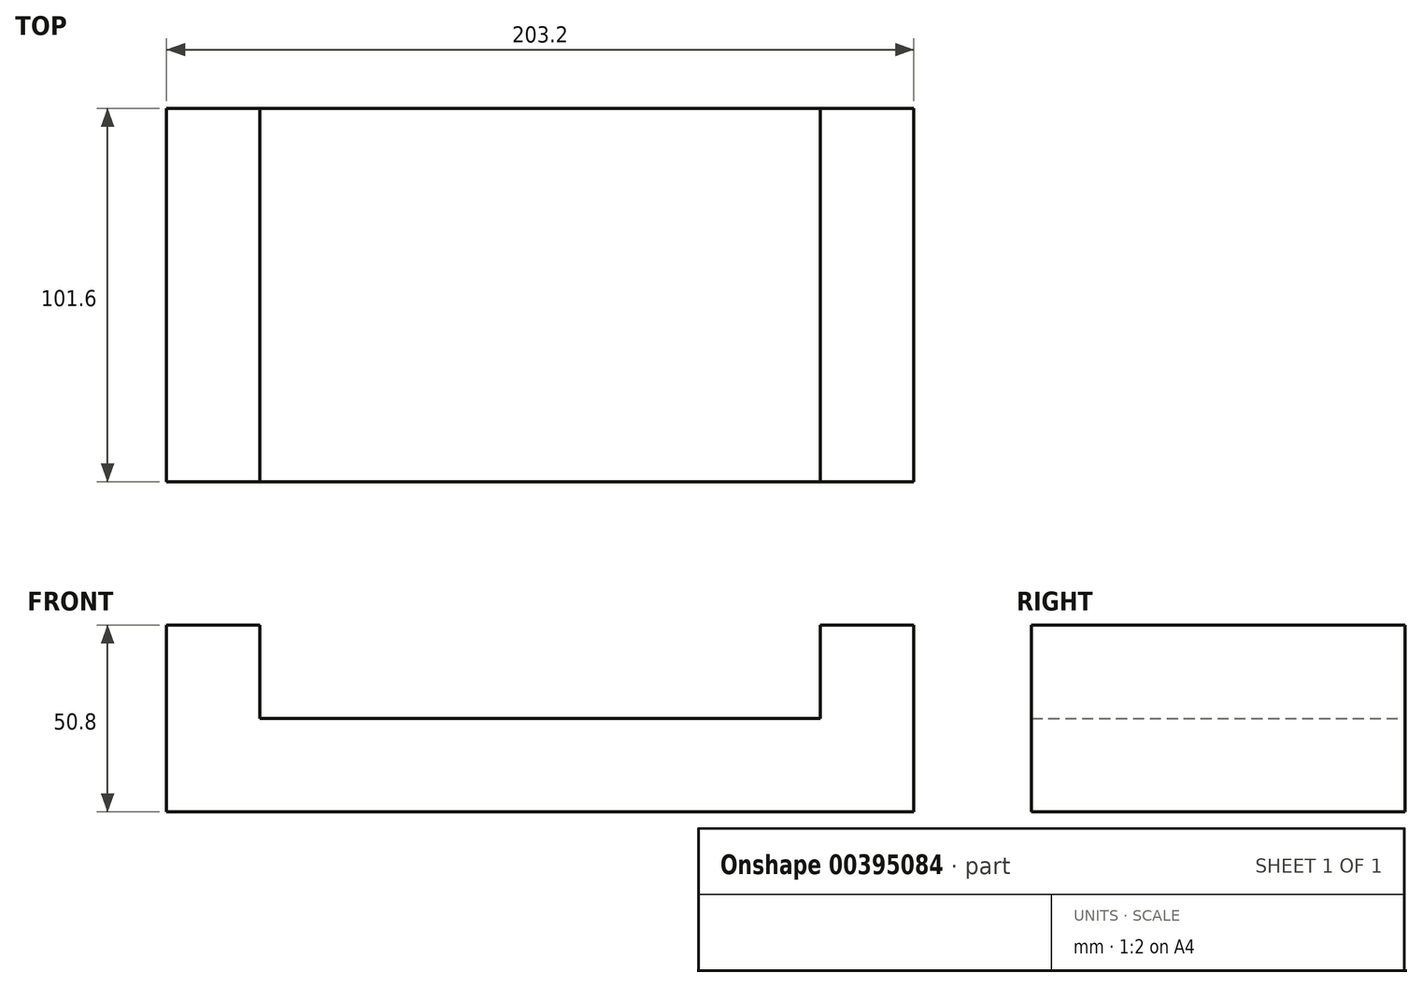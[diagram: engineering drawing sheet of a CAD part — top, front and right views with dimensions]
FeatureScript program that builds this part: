
annotation { "Feature Type Name" : "Feature", "Feature Type Description" : "" }
export const myFeature = defineFeature(function(context is Context, id is Id, definition is map)
    precondition{}
    {
        {
            var Q0;
            Q0=qCreatedBy(makeId("Front.planeOp"),FACE);
            var sketch = newSketch(context, id + "F0", { "sketchPlane" : qUnion([Q0])});
            skLineSegment(sketch, "E0.bottom", {"start": v(-101.6, 0) * mm, "end": v(101.6, 0) * mm});
            skLineSegment(sketch, "E0.left", {"start": v(-101.6, 0) * mm, "end": v(-101.6, 50.8) * mm});
            skLineSegment(sketch, "E0.right", {"start": v(101.6, 0) * mm, "end": v(101.6, 50.8) * mm});
            skLineSegment(sketch, "E1.top", {"start": v(-76.2, 25.4) * mm, "end": v(76.2, 25.4) * mm});
            skLineSegment(sketch, "E1.left", {"start": v(-76.2, 50.8) * mm, "end": v(-76.2, 25.4) * mm});
            skLineSegment(sketch, "E1.right", {"start": v(76.2, 50.8) * mm, "end": v(76.2, 25.4) * mm});
            skLineSegment(sketch, "E2.trimOffspring", {"start": v(76.2, 50.8) * mm, "end": v(101.6, 50.8) * mm});
            skLineSegment(sketch, "E3", {"start": v(-101.6, 50.8) * mm, "end": v(-76.2, 50.8) * mm});
            skSolve(sketch);
        }
        {
            var Q0;
            Q0 = qSketchRegion(id + "F0", true);
            extrude(context, id + "F1", {"entities" : qUnion([Q0]), "depth" : 50.8 * mm, "hasSecondDirection" : true, "secondDirectionOppositeDirection" : true, "secondDirectionDepth" : 50.8 * mm});
        }
    });
